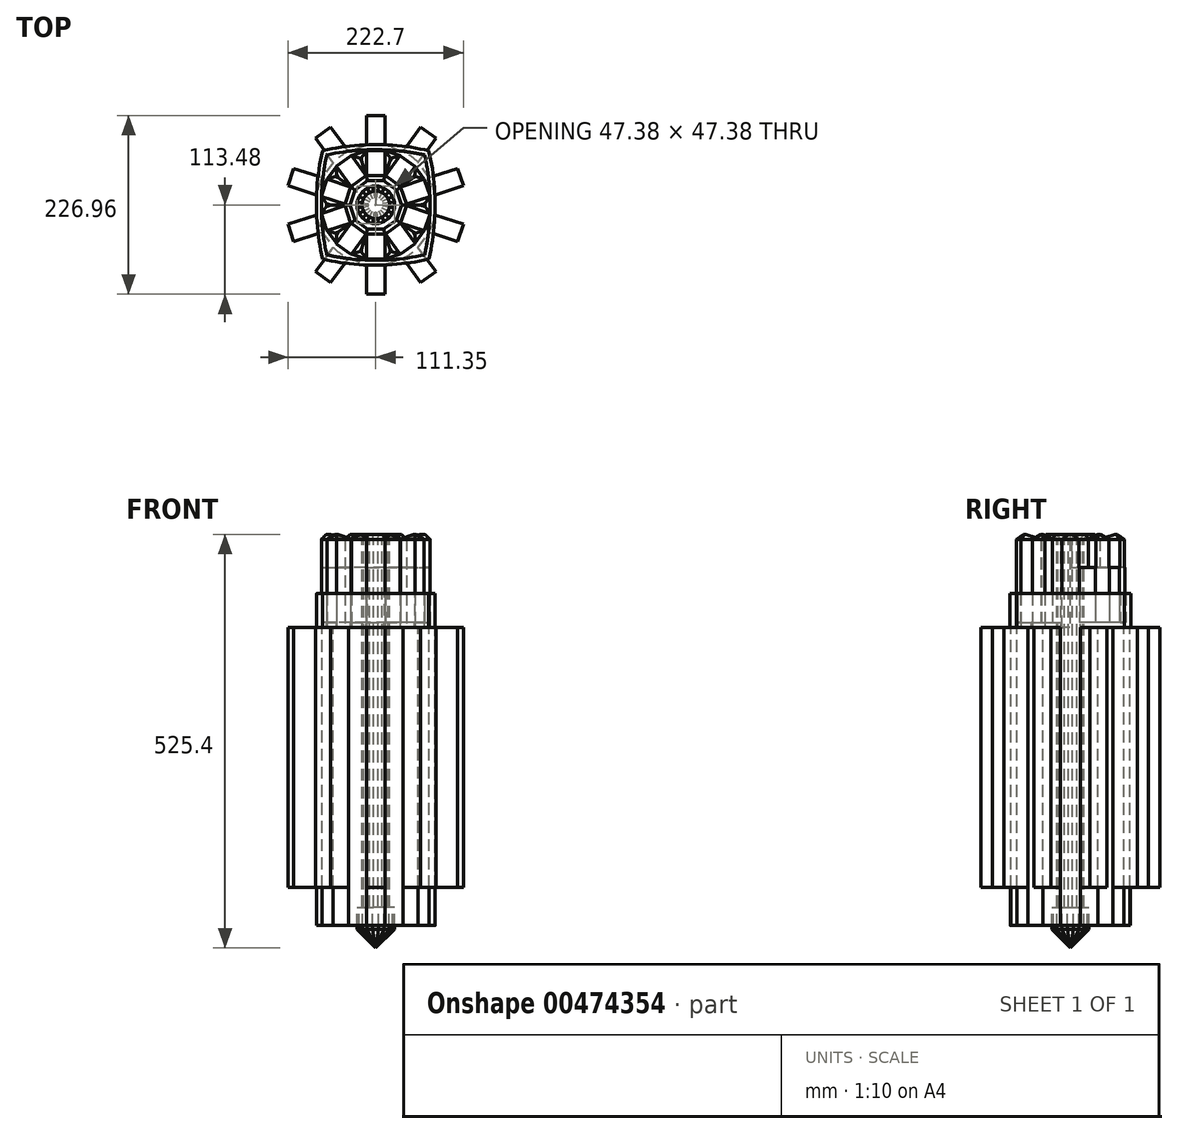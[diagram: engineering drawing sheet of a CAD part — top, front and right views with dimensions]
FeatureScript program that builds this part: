
annotation { "Feature Type Name" : "Feature", "Feature Type Description" : "" }
export const myFeature = defineFeature(function(context is Context, id is Id, definition is map)
    precondition{}
    {
        {
            var Q0;
            Q0=qCreatedBy(makeId("Top.planeOp"),FACE);
            var sketch = newSketch(context, id + "F0", { "sketchPlane" : qUnion([Q0])});
            skEllipse(sketch, "E0", {"center": v(0, 0) * mm, "majorRadius": 152.95 * mm, "minorRadius": 76.53 * mm, "majorAxis": v(1, 0)});
            skEllipse(sketch, "E1", {"center": v(0, 0) * mm, "majorRadius": 153.58 * mm, "minorRadius": 75.38 * mm, "majorAxis": v(0, -1)});
            skEllipse(sketch, "E2", {"center": v(0, 0) * mm, "majorRadius": 194.51 * mm, "minorRadius": 96.8 * mm, "majorAxis": v(0.7, -0.7)});
            skEllipse(sketch, "E3", {"center": v(0, 0) * mm, "majorRadius": 196.36 * mm, "minorRadius": 95.93 * mm, "majorAxis": v(0.7, 0.7)});
            skSolve(sketch);
        }
        {
            var Q0;
            {var subQ0=sQuery(id+"F0.wireOp",EDGE,"E1");var subQ1=sQuery(id+"F0.wireOp",EDGE,"E0");var subQ5=makeQuery(id+"F0.imprint","INTERSECT",VERTEX,{"disambiguationData":[OD(0.0)],"derivedFrom":[subQ1,subQ0]});Q0=makeQuery(id+"F0.imprint","IMPRINT",FACE,{"disambiguationData":[TD([[makeQuery(id+"F0.imprint","IMPRINT",EDGE,{"disambiguationData":[TD([[subQ5,-1.0]])],"derivedFrom":subQ1}),1.0]])]});}
            extrude(context, id + "F1", {"entities" : qUnion([Q0]), "depth" : 127 * mm});
        }
        {
            var Q0;
            Q0=makeQuery(id+"F1.opExtrude","CAP_FACE",FACE,{"disambiguationData":[OSD([sQuery(id+"F0.wireOp",EDGE,"E0"),sQuery(id+"F0.wireOp",EDGE,"E1"),sQuery(id+"F0.wireOp",EDGE,"E3")])],"isStart":true});
            var sketch = newSketch(context, id + "F2", { "sketchPlane" : qUnion([Q0])});
            skCircle(sketch, "E4.cCircle", {"center": v(0, 0) * mm, "radius": 75.38 * mm, "construction": true});
            skLineSegment(sketch, "E4.0", {"start": v(75.38, 11.94) * mm, "end": v(75.38, -11.94) * mm});
            skLineSegment(sketch, "E4.1", {"start": v(75.38, -11.94) * mm, "end": v(68, -34.65) * mm});
            skLineSegment(sketch, "E4.2", {"start": v(68, -34.65) * mm, "end": v(53.96, -53.96) * mm});
            skLineSegment(sketch, "E4.3", {"start": v(53.96, -53.96) * mm, "end": v(34.65, -68) * mm});
            skLineSegment(sketch, "E4.4", {"start": v(34.65, -68) * mm, "end": v(11.94, -75.38) * mm});
            skLineSegment(sketch, "E4.5", {"start": v(11.94, -75.38) * mm, "end": v(-11.94, -75.38) * mm});
            skLineSegment(sketch, "E4.6", {"start": v(-11.94, -75.38) * mm, "end": v(-34.65, -68) * mm});
            skLineSegment(sketch, "E4.7", {"start": v(-34.65, -68) * mm, "end": v(-53.96, -53.96) * mm});
            skLineSegment(sketch, "E4.8", {"start": v(-53.96, -53.96) * mm, "end": v(-68, -34.65) * mm});
            skLineSegment(sketch, "E4.9", {"start": v(-68, -34.65) * mm, "end": v(-75.38, -11.94) * mm});
            skLineSegment(sketch, "E4.10", {"start": v(-75.38, -11.94) * mm, "end": v(-75.38, 11.94) * mm});
            skLineSegment(sketch, "E4.11", {"start": v(-75.38, 11.94) * mm, "end": v(-68, 34.65) * mm});
            skLineSegment(sketch, "E4.12", {"start": v(-68, 34.65) * mm, "end": v(-53.96, 53.96) * mm});
            skLineSegment(sketch, "E4.13", {"start": v(-53.96, 53.96) * mm, "end": v(-34.65, 68) * mm});
            skLineSegment(sketch, "E4.14", {"start": v(-34.65, 68) * mm, "end": v(-11.94, 75.38) * mm});
            skLineSegment(sketch, "E4.15", {"start": v(-11.94, 75.38) * mm, "end": v(11.94, 75.38) * mm});
            skLineSegment(sketch, "E4.16", {"start": v(11.94, 75.38) * mm, "end": v(34.65, 68) * mm});
            skLineSegment(sketch, "E4.17", {"start": v(34.65, 68) * mm, "end": v(53.96, 53.96) * mm});
            skLineSegment(sketch, "E4.18", {"start": v(53.96, 53.96) * mm, "end": v(68, 34.65) * mm});
            skLineSegment(sketch, "E4.19", {"start": v(68, 34.65) * mm, "end": v(75.38, 11.94) * mm});
            skPoint(sketch, "E4.0.midPoint", {"position": v(75.38, 0) * mm});
            skSolve(sketch);
        }
        {
            var Q0;
            {var subQ11=sQuery(id+"F2.wireOp",EDGE,"E4.2");Q0=makeQuery(id+"F2.imprint","IMPRINT",FACE,{"disambiguationData":[TD([[makeQuery(id+"F2.imprint","IMPRINT",EDGE,{"derivedFrom":subQ11}),-1.0]])]});}
            extrude(context, id + "F3", {"entities" : qUnion([Q0]), "operationType" : NewBodyOperationType.ADD, "depth" : 76.2 * mm});
        }
        {
            var Q0;
            Q0=makeQuery(id+"F3.opExtrude","CAP_FACE",FACE,{"disambiguationData":[OSD([sQuery(id+"F0.wireOp",EDGE,"E1"),sQuery(id+"F2.wireOp",EDGE,"E4.1"),sQuery(id+"F2.wireOp",EDGE,"E4.2"),sQuery(id+"F2.wireOp",EDGE,"E4.3"),sQuery(id+"F2.wireOp",EDGE,"E4.4"),sQuery(id+"F2.wireOp",EDGE,"E4.5"),sQuery(id+"F2.wireOp",EDGE,"E4.6"),sQuery(id+"F2.wireOp",EDGE,"E4.7"),sQuery(id+"F2.wireOp",EDGE,"E4.8"),sQuery(id+"F2.wireOp",EDGE,"E4.9"),sQuery(id+"F2.wireOp",EDGE,"E4.11"),sQuery(id+"F2.wireOp",EDGE,"E4.12"),sQuery(id+"F2.wireOp",EDGE,"E4.13"),sQuery(id+"F2.wireOp",EDGE,"E4.14"),sQuery(id+"F2.wireOp",EDGE,"E4.15"),sQuery(id+"F2.wireOp",EDGE,"E4.16"),sQuery(id+"F2.wireOp",EDGE,"E4.17"),sQuery(id+"F2.wireOp",EDGE,"E4.18"),sQuery(id+"F2.wireOp",EDGE,"E4.19")])],"isStart":false});
            var sketch = newSketch(context, id + "F4", { "sketchPlane" : qUnion([Q0])});
            skCircle(sketch, "E5.cCircle", {"center": v(0, 0) * mm, "radius": 23.7 * mm, "construction": true});
            skPoint(sketch, "E5.cCircle.perimeterSnap0", {"position": v(71.56, -23.7) * mm});
            skLineSegment(sketch, "E5.0", {"start": v(3.75, -23.7) * mm, "end": v(-3.75, -23.7) * mm});
            skLineSegment(sketch, "E5.1", {"start": v(-3.75, -23.7) * mm, "end": v(-10.9, -21.37) * mm});
            skLineSegment(sketch, "E5.2", {"start": v(-10.9, -21.37) * mm, "end": v(-16.96, -16.96) * mm});
            skLineSegment(sketch, "E5.3", {"start": v(-16.96, -16.96) * mm, "end": v(-21.37, -10.9) * mm});
            skLineSegment(sketch, "E5.4", {"start": v(-21.37, -10.9) * mm, "end": v(-23.7, -3.75) * mm});
            skLineSegment(sketch, "E5.5", {"start": v(-23.7, -3.75) * mm, "end": v(-23.7, 3.75) * mm});
            skLineSegment(sketch, "E5.6", {"start": v(-23.7, 3.75) * mm, "end": v(-21.37, 10.9) * mm});
            skLineSegment(sketch, "E5.7", {"start": v(-21.37, 10.9) * mm, "end": v(-16.96, 16.96) * mm});
            skLineSegment(sketch, "E5.8", {"start": v(-16.96, 16.96) * mm, "end": v(-10.9, 21.37) * mm});
            skLineSegment(sketch, "E5.9", {"start": v(-10.9, 21.37) * mm, "end": v(-3.75, 23.7) * mm});
            skLineSegment(sketch, "E5.10", {"start": v(-3.75, 23.7) * mm, "end": v(3.75, 23.7) * mm});
            skLineSegment(sketch, "E5.11", {"start": v(3.75, 23.7) * mm, "end": v(10.9, 21.37) * mm});
            skLineSegment(sketch, "E5.12", {"start": v(10.9, 21.37) * mm, "end": v(16.96, 16.96) * mm});
            skLineSegment(sketch, "E5.13", {"start": v(16.96, 16.96) * mm, "end": v(21.37, 10.9) * mm});
            skLineSegment(sketch, "E5.14", {"start": v(21.37, 10.9) * mm, "end": v(23.7, 3.75) * mm});
            skLineSegment(sketch, "E5.15", {"start": v(23.7, 3.75) * mm, "end": v(23.7, -3.75) * mm});
            skLineSegment(sketch, "E5.16", {"start": v(23.7, -3.75) * mm, "end": v(21.37, -10.9) * mm});
            skLineSegment(sketch, "E5.17", {"start": v(21.37, -10.9) * mm, "end": v(16.96, -16.96) * mm});
            skLineSegment(sketch, "E5.18", {"start": v(16.96, -16.96) * mm, "end": v(10.9, -21.37) * mm});
            skLineSegment(sketch, "E5.19", {"start": v(10.9, -21.37) * mm, "end": v(3.75, -23.7) * mm});
            skPoint(sketch, "E5.0.midPoint", {"position": v(0, -23.7) * mm});
            skPoint(sketch, "E5.0.midPoint.positionSnap0", {"position": v(71.56, -23.7) * mm});
            skSolve(sketch);
        }
        {
            var Q0;
            Q0=makeQuery(id+"F4.imprint","IMPRINT",FACE,{"disambiguationData":[TD([[makeQuery(id+"F4.imprint","IMPRINT",EDGE,{"derivedFrom":sQuery(id+"F4.wireOp",EDGE,"E5.0")}),-1.0]])]});
            extrude(context, id + "F5", {"entities" : qUnion([Q0]), "operationType" : NewBodyOperationType.ADD, "depth" : 25.4 * mm});
        }
        {
            var Q0;
            Q0=makeQuery(id+"F5.opExtrude","CAP_FACE",FACE,{"disambiguationData":[OSD([sQuery(id+"F4.wireOp",EDGE,"E5.0"),sQuery(id+"F4.wireOp",EDGE,"E5.1"),sQuery(id+"F4.wireOp",EDGE,"E5.2"),sQuery(id+"F4.wireOp",EDGE,"E5.3"),sQuery(id+"F4.wireOp",EDGE,"E5.4"),sQuery(id+"F4.wireOp",EDGE,"E5.5"),sQuery(id+"F4.wireOp",EDGE,"E5.6"),sQuery(id+"F4.wireOp",EDGE,"E5.7"),sQuery(id+"F4.wireOp",EDGE,"E5.8"),sQuery(id+"F4.wireOp",EDGE,"E5.9"),sQuery(id+"F4.wireOp",EDGE,"E5.10"),sQuery(id+"F4.wireOp",EDGE,"E5.11"),sQuery(id+"F4.wireOp",EDGE,"E5.12"),sQuery(id+"F4.wireOp",EDGE,"E5.13"),sQuery(id+"F4.wireOp",EDGE,"E5.14"),sQuery(id+"F4.wireOp",EDGE,"E5.15"),sQuery(id+"F4.wireOp",EDGE,"E5.16"),sQuery(id+"F4.wireOp",EDGE,"E5.17"),sQuery(id+"F4.wireOp",EDGE,"E5.18"),sQuery(id+"F4.wireOp",EDGE,"E5.19")])],"isStart":false});
            shell(context, id + "F6", {"entities" : qUnion([Q0]), "thickness" : 6.35 * mm});
        }
        {
            var Q0;
            Q0=makeQuery(id+"F3.opExtrude","CAP_FACE",FACE,{"disambiguationData":[OSD([sQuery(id+"F0.wireOp",EDGE,"E1"),sQuery(id+"F2.wireOp",EDGE,"E4.1"),sQuery(id+"F2.wireOp",EDGE,"E4.2"),sQuery(id+"F2.wireOp",EDGE,"E4.3"),sQuery(id+"F2.wireOp",EDGE,"E4.4"),sQuery(id+"F2.wireOp",EDGE,"E4.5"),sQuery(id+"F2.wireOp",EDGE,"E4.6"),sQuery(id+"F2.wireOp",EDGE,"E4.7"),sQuery(id+"F2.wireOp",EDGE,"E4.8"),sQuery(id+"F2.wireOp",EDGE,"E4.9"),sQuery(id+"F2.wireOp",EDGE,"E4.11"),sQuery(id+"F2.wireOp",EDGE,"E4.12"),sQuery(id+"F2.wireOp",EDGE,"E4.13"),sQuery(id+"F2.wireOp",EDGE,"E4.14"),sQuery(id+"F2.wireOp",EDGE,"E4.15"),sQuery(id+"F2.wireOp",EDGE,"E4.16"),sQuery(id+"F2.wireOp",EDGE,"E4.17"),sQuery(id+"F2.wireOp",EDGE,"E4.18"),sQuery(id+"F2.wireOp",EDGE,"E4.19")])],"isStart":false});
            extrude(context, id + "F7", {"entities" : qUnion([Q0]), "operationType" : NewBodyOperationType.ADD, "depth" : 254 * mm});
        }
        {
            var Q0;
            Q0=makeQuery(id+"F5.opExtrude","CAP_FACE",FACE,{"disambiguationData":[OSD([sQuery(id+"F4.wireOp",EDGE,"E5.0"),sQuery(id+"F4.wireOp",EDGE,"E5.1"),sQuery(id+"F4.wireOp",EDGE,"E5.2"),sQuery(id+"F4.wireOp",EDGE,"E5.3"),sQuery(id+"F4.wireOp",EDGE,"E5.4"),sQuery(id+"F4.wireOp",EDGE,"E5.5"),sQuery(id+"F4.wireOp",EDGE,"E5.6"),sQuery(id+"F4.wireOp",EDGE,"E5.7"),sQuery(id+"F4.wireOp",EDGE,"E5.8"),sQuery(id+"F4.wireOp",EDGE,"E5.9"),sQuery(id+"F4.wireOp",EDGE,"E5.10"),sQuery(id+"F4.wireOp",EDGE,"E5.11"),sQuery(id+"F4.wireOp",EDGE,"E5.12"),sQuery(id+"F4.wireOp",EDGE,"E5.13"),sQuery(id+"F4.wireOp",EDGE,"E5.14"),sQuery(id+"F4.wireOp",EDGE,"E5.15"),sQuery(id+"F4.wireOp",EDGE,"E5.16"),sQuery(id+"F4.wireOp",EDGE,"E5.17"),sQuery(id+"F4.wireOp",EDGE,"E5.18"),sQuery(id+"F4.wireOp",EDGE,"E5.19")])],"isStart":false});
            extrude(context, id + "F8", {"entities" : qUnion([Q0]), "operationType" : NewBodyOperationType.ADD, "depth" : 254 * mm});
        }
        {
            var Q0;
            {var subQ0=sQuery(id+"F2.wireOp",EDGE,"E4.5");Q0=makeQuery(id+"F7.boolean.opBoolean","MERGE",FACE,{"derivedFrom":[makeQuery(id+"F3.opExtrude","SWEPT_FACE",FACE,{"disambiguationData":[OSD([subQ0])]}),makeQuery(id+"F7.opExtrude","SWEPT_FACE",FACE,{"disambiguationData":[OSD([subQ0])]})]});}
            var Q1;
            {var subQ0=sQuery(id+"F2.wireOp",EDGE,"E4.15");Q1=makeQuery(id+"F7.boolean.opBoolean","MERGE",FACE,{"derivedFrom":[makeQuery(id+"F3.opExtrude","SWEPT_FACE",FACE,{"disambiguationData":[OSD([subQ0])]}),makeQuery(id+"F7.opExtrude","SWEPT_FACE",FACE,{"disambiguationData":[OSD([subQ0])]})]});}
            extrude(context, id + "F9", {"entities" : qUnion([Q0, Q1]), "operationType" : NewBodyOperationType.ADD, "endBound" : BoundingType.SYMMETRIC, "depth" : 76.2 * mm});
        }
        {
            var Q0;
            {var subQ0=sQuery(id+"F2.wireOp",EDGE,"E4.13");Q0=makeQuery(id+"F7.boolean.opBoolean","MERGE",FACE,{"derivedFrom":[makeQuery(id+"F3.opExtrude","SWEPT_FACE",FACE,{"disambiguationData":[OSD([subQ0])]}),makeQuery(id+"F7.opExtrude","SWEPT_FACE",FACE,{"disambiguationData":[OSD([subQ0])]})]});}
            var Q1;
            {var subQ0=sQuery(id+"F2.wireOp",EDGE,"E4.3");Q1=makeQuery(id+"F7.boolean.opBoolean","MERGE",FACE,{"derivedFrom":[makeQuery(id+"F3.opExtrude","SWEPT_FACE",FACE,{"disambiguationData":[OSD([subQ0])]}),makeQuery(id+"F7.opExtrude","SWEPT_FACE",FACE,{"disambiguationData":[OSD([subQ0])]})]});}
            extrude(context, id + "F10", {"entities" : qUnion([Q0, Q1]), "operationType" : NewBodyOperationType.ADD, "endBound" : BoundingType.SYMMETRIC, "depth" : 76.2 * mm});
        }
        {
            var Q0;
            {var subQ0=sQuery(id+"F2.wireOp",EDGE,"E4.17");Q0=makeQuery(id+"F7.boolean.opBoolean","MERGE",FACE,{"derivedFrom":[makeQuery(id+"F3.opExtrude","SWEPT_FACE",FACE,{"disambiguationData":[OSD([subQ0])]}),makeQuery(id+"F7.opExtrude","SWEPT_FACE",FACE,{"disambiguationData":[OSD([subQ0])]})]});}
            var Q1;
            {var subQ0=sQuery(id+"F2.wireOp",EDGE,"E4.7");Q1=makeQuery(id+"F7.boolean.opBoolean","MERGE",FACE,{"derivedFrom":[makeQuery(id+"F3.opExtrude","SWEPT_FACE",FACE,{"disambiguationData":[OSD([subQ0])]}),makeQuery(id+"F7.opExtrude","SWEPT_FACE",FACE,{"disambiguationData":[OSD([subQ0])]})]});}
            extrude(context, id + "F11", {"entities" : qUnion([Q0, Q1]), "operationType" : NewBodyOperationType.ADD, "endBound" : BoundingType.SYMMETRIC, "depth" : 76.2 * mm});
        }
        {
            var Q0;
            {var subQ0=sQuery(id+"F2.wireOp",EDGE,"E4.9");Q0=makeQuery(id+"F7.boolean.opBoolean","MERGE",FACE,{"derivedFrom":[makeQuery(id+"F3.opExtrude","SWEPT_FACE",FACE,{"disambiguationData":[OSD([subQ0])]}),makeQuery(id+"F7.opExtrude","SWEPT_FACE",FACE,{"disambiguationData":[OSD([subQ0])]})]});}
            var Q1;
            {var subQ0=sQuery(id+"F2.wireOp",EDGE,"E4.19");Q1=makeQuery(id+"F7.boolean.opBoolean","MERGE",FACE,{"derivedFrom":[makeQuery(id+"F3.opExtrude","SWEPT_FACE",FACE,{"disambiguationData":[OSD([subQ0])]}),makeQuery(id+"F7.opExtrude","SWEPT_FACE",FACE,{"disambiguationData":[OSD([subQ0])]})]});}
            extrude(context, id + "F12", {"entities" : qUnion([Q0, Q1]), "operationType" : NewBodyOperationType.ADD, "endBound" : BoundingType.SYMMETRIC, "depth" : 76.2 * mm});
        }
        {
            var Q0;
            {var subQ0=sQuery(id+"F2.wireOp",EDGE,"E4.11");Q0=makeQuery(id+"F7.boolean.opBoolean","MERGE",FACE,{"derivedFrom":[makeQuery(id+"F3.opExtrude","SWEPT_FACE",FACE,{"disambiguationData":[OSD([subQ0])]}),makeQuery(id+"F7.opExtrude","SWEPT_FACE",FACE,{"disambiguationData":[OSD([subQ0])]})]});}
            var Q1;
            {var subQ0=sQuery(id+"F2.wireOp",EDGE,"E4.1");Q1=makeQuery(id+"F7.boolean.opBoolean","MERGE",FACE,{"derivedFrom":[makeQuery(id+"F3.opExtrude","SWEPT_FACE",FACE,{"disambiguationData":[OSD([subQ0])]}),makeQuery(id+"F7.opExtrude","SWEPT_FACE",FACE,{"disambiguationData":[OSD([subQ0])]})]});}
            extrude(context, id + "F13", {"entities" : qUnion([Q0, Q1]), "operationType" : NewBodyOperationType.ADD, "endBound" : BoundingType.SYMMETRIC, "depth" : 76.2 * mm});
        }
        {
            var Q0;
            Q0=makeQuery(id+"F1.opExtrude","CAP_FACE",FACE,{"disambiguationData":[OSD([sQuery(id+"F0.wireOp",EDGE,"E0"),sQuery(id+"F0.wireOp",EDGE,"E1"),sQuery(id+"F0.wireOp",EDGE,"E3")])],"isStart":false});
            extrude(context, id + "F14", {"entities" : qUnion([Q0]), "operationType" : NewBodyOperationType.REMOVE, "endBound" : BoundingType.SYMMETRIC, "oppositeDirection" : true, "depth" : 168.38 * mm});
        }
        {
            var Q0;
            {var subQ0=sQuery(id+"F2.wireOp",EDGE,"E4.3");var subQ1=sQuery(id+"F2.wireOp",EDGE,"E4.2");Q0=makeQuery(id+"F10.boolean.opBoolean","SPLIT",FACE,{"disambiguationData":[TD([makeQuery(id+"F6.opShell","OFFSET_FACE",FACE,{"disambiguationData":[OSD([subQ1])]})])],"derivedFrom":makeQuery(id+"F10.opExtrude","SWEPT_FACE",FACE,{"disambiguationData":[OSD([subQ0]),TDD([makeQuery(id+"F3.opExtrude","CAP_EDGE",EDGE,{"disambiguationData":[OSD([subQ0])],"isStart":true})])]})});}
            var Q1;
            {var subQ0=sQuery(id+"F2.wireOp",EDGE,"E4.5");var subQ1=sQuery(id+"F2.wireOp",EDGE,"E4.4");Q1=makeQuery(id+"F9.boolean.opBoolean","SPLIT",FACE,{"disambiguationData":[TD([makeQuery(id+"F6.opShell","OFFSET_FACE",FACE,{"disambiguationData":[OSD([subQ1])]})])],"derivedFrom":makeQuery(id+"F9.opExtrude","SWEPT_FACE",FACE,{"disambiguationData":[OSD([subQ0]),TDD([makeQuery(id+"F3.opExtrude","CAP_EDGE",EDGE,{"disambiguationData":[OSD([subQ0])],"isStart":true})])]})});}
            var Q2;
            {var subQ1=sQuery(id+"F2.wireOp",EDGE,"E4.7");var subQ2=sQuery(id+"F2.wireOp",EDGE,"E4.6");Q2=makeQuery(id+"F11.boolean.opBoolean","SPLIT",FACE,{"disambiguationData":[TD([makeQuery(id+"F6.opShell","OFFSET_FACE",FACE,{"disambiguationData":[OSD([subQ2])]})])],"derivedFrom":makeQuery(id+"F11.opExtrude","SWEPT_FACE",FACE,{"disambiguationData":[OSD([subQ1]),TDD([makeQuery(id+"F3.opExtrude","CAP_EDGE",EDGE,{"disambiguationData":[OSD([subQ1])],"isStart":true})])]})});}
            var Q3;
            {var subQ4=sQuery(id+"F2.wireOp",EDGE,"E4.9");var subQ5=sQuery(id+"F2.wireOp",EDGE,"E4.8");Q3=makeQuery(id+"F12.boolean.opBoolean","SPLIT",FACE,{"disambiguationData":[TD([makeQuery(id+"F6.opShell","OFFSET_FACE",FACE,{"disambiguationData":[OSD([subQ5])]})])],"derivedFrom":makeQuery(id+"F12.opExtrude","SWEPT_FACE",FACE,{"disambiguationData":[OSD([subQ4]),TDD([makeQuery(id+"F3.opExtrude","CAP_EDGE",EDGE,{"disambiguationData":[OSD([subQ4])],"isStart":true})])]})});}
            var Q4;
            {var subQ1=sQuery(id+"F2.wireOp",EDGE,"E4.15");var subQ2=sQuery(id+"F2.wireOp",EDGE,"E4.14");Q4=makeQuery(id+"F9.boolean.opBoolean","SPLIT",FACE,{"disambiguationData":[TD([makeQuery(id+"F6.opShell","OFFSET_FACE",FACE,{"disambiguationData":[OSD([subQ2])]})])],"derivedFrom":makeQuery(id+"F9.opExtrude","SWEPT_FACE",FACE,{"disambiguationData":[OSD([subQ1]),TDD([makeQuery(id+"F3.opExtrude","CAP_EDGE",EDGE,{"disambiguationData":[OSD([subQ1])],"isStart":true})])]})});}
            var Q5;
            {var subQ0=sQuery(id+"F2.wireOp",EDGE,"E4.17");var subQ1=sQuery(id+"F2.wireOp",EDGE,"E4.16");Q5=makeQuery(id+"F11.boolean.opBoolean","SPLIT",FACE,{"disambiguationData":[TD([makeQuery(id+"F6.opShell","OFFSET_FACE",FACE,{"disambiguationData":[OSD([subQ1])]})])],"derivedFrom":makeQuery(id+"F11.opExtrude","SWEPT_FACE",FACE,{"disambiguationData":[OSD([subQ0]),TDD([makeQuery(id+"F3.opExtrude","CAP_EDGE",EDGE,{"disambiguationData":[OSD([subQ0])],"isStart":true})])]})});}
            var Q6;
            {var subQ1=sQuery(id+"F2.wireOp",EDGE,"E4.11");Q6=makeQuery(id+"F13.boolean.opBoolean","SPLIT",FACE,{"disambiguationData":[TD([makeQuery(id+"F6.opShell","OFFSET_FACE",FACE,{"disambiguationData":[OSD([subQ1])]})])],"derivedFrom":makeQuery(id+"F13.opExtrude","SWEPT_FACE",FACE,{"disambiguationData":[OSD([subQ1]),TDD([makeQuery(id+"F3.opExtrude","CAP_EDGE",EDGE,{"disambiguationData":[OSD([subQ1])],"isStart":true})])]})});}
            var Q7;
            {var subQ1=sQuery(id+"F2.wireOp",EDGE,"E4.13");var subQ2=sQuery(id+"F2.wireOp",EDGE,"E4.12");Q7=makeQuery(id+"F10.boolean.opBoolean","SPLIT",FACE,{"disambiguationData":[TD([makeQuery(id+"F6.opShell","OFFSET_FACE",FACE,{"disambiguationData":[OSD([subQ2])]})])],"derivedFrom":makeQuery(id+"F10.opExtrude","SWEPT_FACE",FACE,{"disambiguationData":[OSD([subQ1]),TDD([makeQuery(id+"F3.opExtrude","CAP_EDGE",EDGE,{"disambiguationData":[OSD([subQ1])],"isStart":true})])]})});}
            var Q8;
            {var subQ1=sQuery(id+"F2.wireOp",EDGE,"E4.1");Q8=makeQuery(id+"F13.boolean.opBoolean","SPLIT",FACE,{"disambiguationData":[TD([makeQuery(id+"F6.opShell","OFFSET_FACE",FACE,{"disambiguationData":[OSD([subQ1])]})])],"derivedFrom":makeQuery(id+"F13.opExtrude","SWEPT_FACE",FACE,{"disambiguationData":[OSD([subQ1]),TDD([makeQuery(id+"F3.opExtrude","CAP_EDGE",EDGE,{"disambiguationData":[OSD([subQ1])],"isStart":true})])]})});}
            var Q9;
            {var subQ0=sQuery(id+"F2.wireOp",EDGE,"E4.19");var subQ1=sQuery(id+"F2.wireOp",EDGE,"E4.18");Q9=makeQuery(id+"F12.boolean.opBoolean","SPLIT",FACE,{"disambiguationData":[TD([makeQuery(id+"F6.opShell","OFFSET_FACE",FACE,{"disambiguationData":[OSD([subQ1])]})])],"derivedFrom":makeQuery(id+"F12.opExtrude","SWEPT_FACE",FACE,{"disambiguationData":[OSD([subQ0]),TDD([makeQuery(id+"F3.opExtrude","CAP_EDGE",EDGE,{"disambiguationData":[OSD([subQ0])],"isStart":true})])]})});}
            extrude(context, id + "F15", {"entities" : qUnion([Q0, Q1, Q2, Q3, Q4, Q5, Q6, Q7, Q8, Q9]), "operationType" : NewBodyOperationType.ADD, "depth" : 71.7 * mm});
        }
        {
            var Q0;
            Q0=makeQuery(id+"F6.opShell","OFFSET_FACE",FACE,{"disambiguationData":[OSD([sQuery(id+"F0.wireOp",EDGE,"E1"),sQuery(id+"F2.wireOp",EDGE,"E4.1"),sQuery(id+"F2.wireOp",EDGE,"E4.2"),sQuery(id+"F2.wireOp",EDGE,"E4.3"),sQuery(id+"F2.wireOp",EDGE,"E4.4"),sQuery(id+"F2.wireOp",EDGE,"E4.5"),sQuery(id+"F2.wireOp",EDGE,"E4.6"),sQuery(id+"F2.wireOp",EDGE,"E4.7"),sQuery(id+"F2.wireOp",EDGE,"E4.8"),sQuery(id+"F2.wireOp",EDGE,"E4.9"),sQuery(id+"F2.wireOp",EDGE,"E4.11"),sQuery(id+"F2.wireOp",EDGE,"E4.12"),sQuery(id+"F2.wireOp",EDGE,"E4.13"),sQuery(id+"F2.wireOp",EDGE,"E4.14"),sQuery(id+"F2.wireOp",EDGE,"E4.15"),sQuery(id+"F2.wireOp",EDGE,"E4.16"),sQuery(id+"F2.wireOp",EDGE,"E4.17"),sQuery(id+"F2.wireOp",EDGE,"E4.18"),sQuery(id+"F2.wireOp",EDGE,"E4.19")])]});
            extrude(context, id + "F16", {"entities" : qUnion([Q0]), "operationType" : NewBodyOperationType.ADD, "endBound" : BoundingType.SYMMETRIC, "depth" : 376 * mm});
        }
        {
            var Q0;
            Q0=makeQuery(id+"F15.opExtrude","CAP_FACE",FACE,{"disambiguationData":[OSD([sQuery(id+"F2.wireOp",EDGE,"E4.9")])],"isStart":false});
            var Q1;
            Q1=makeQuery(id+"F15.opExtrude","CAP_FACE",FACE,{"disambiguationData":[OSD([sQuery(id+"F2.wireOp",EDGE,"E4.3")])],"isStart":false});
            var Q2;
            Q2=makeQuery(id+"F15.opExtrude","CAP_FACE",FACE,{"disambiguationData":[OSD([sQuery(id+"F2.wireOp",EDGE,"E4.17")])],"isStart":false});
            var Q3;
            Q3=makeQuery(id+"F15.opExtrude","CAP_FACE",FACE,{"disambiguationData":[OSD([sQuery(id+"F2.wireOp",EDGE,"E4.11")])],"isStart":false});
            var Q4;
            Q4=makeQuery(id+"F15.opExtrude","CAP_FACE",FACE,{"disambiguationData":[OSD([sQuery(id+"F2.wireOp",EDGE,"E4.13")])],"isStart":false});
            var Q5;
            Q5=makeQuery(id+"F15.opExtrude","CAP_FACE",FACE,{"disambiguationData":[OSD([sQuery(id+"F2.wireOp",EDGE,"E4.15")])],"isStart":false});
            var Q6;
            Q6=makeQuery(id+"F15.opExtrude","CAP_FACE",FACE,{"disambiguationData":[OSD([sQuery(id+"F2.wireOp",EDGE,"E4.1")])],"isStart":false});
            var Q7;
            Q7=makeQuery(id+"F15.opExtrude","CAP_FACE",FACE,{"disambiguationData":[OSD([sQuery(id+"F2.wireOp",EDGE,"E4.19")])],"isStart":false});
            var Q8;
            Q8=makeQuery(id+"F15.opExtrude","CAP_FACE",FACE,{"disambiguationData":[OSD([sQuery(id+"F2.wireOp",EDGE,"E4.5")])],"isStart":false});
            var Q9;
            Q9=makeQuery(id+"F15.opExtrude","CAP_FACE",FACE,{"disambiguationData":[OSD([sQuery(id+"F2.wireOp",EDGE,"E4.7")])],"isStart":false});
            extrude(context, id + "F17", {"entities" : qUnion([Q0, Q1, Q2, Q3, Q4, Q5, Q6, Q7, Q8, Q9]), "operationType" : NewBodyOperationType.ADD, "endBound" : BoundingType.SYMMETRIC, "depth" : 8.15 * mm});
        }
        {
            var Q0;
            {var subQ0=sQuery(id+"F2.wireOp",EDGE,"E4.11");var subQ1=sQuery(id+"F2.wireOp",EDGE,"E4.1");var subQ2=sQuery(id+"F2.wireOp",EDGE,"E4.19");var subQ3=sQuery(id+"F2.wireOp",EDGE,"E4.9");var subQ4=sQuery(id+"F2.wireOp",EDGE,"E4.17");var subQ5=sQuery(id+"F2.wireOp",EDGE,"E4.7");var subQ6=sQuery(id+"F2.wireOp",EDGE,"E4.13");var subQ7=sQuery(id+"F2.wireOp",EDGE,"E4.3");var subQ8=sQuery(id+"F2.wireOp",EDGE,"E4.15");var subQ9=sQuery(id+"F2.wireOp",EDGE,"E4.5");Q0=makeQuery(id+"F13.boolean.opBoolean","MERGE",FACE,{"derivedFrom":[makeQuery(id+"F12.boolean.opBoolean","MERGE",FACE,{"derivedFrom":[makeQuery(id+"F11.boolean.opBoolean","MERGE",FACE,{"derivedFrom":[makeQuery(id+"F10.boolean.opBoolean","MERGE",FACE,{"derivedFrom":[makeQuery(id+"F9.boolean.opBoolean","MERGE",FACE,{"derivedFrom":[makeQuery(id+"F7.opExtrude","CAP_FACE",FACE,{"disambiguationData":[OSD([sQuery(id+"F0.wireOp",EDGE,"E1"),subQ1,sQuery(id+"F2.wireOp",EDGE,"E4.2"),subQ7,sQuery(id+"F2.wireOp",EDGE,"E4.4"),subQ9,sQuery(id+"F2.wireOp",EDGE,"E4.6"),subQ5,sQuery(id+"F2.wireOp",EDGE,"E4.8"),subQ3,subQ0,sQuery(id+"F2.wireOp",EDGE,"E4.12"),subQ6,sQuery(id+"F2.wireOp",EDGE,"E4.14"),subQ8,sQuery(id+"F2.wireOp",EDGE,"E4.16"),subQ4,sQuery(id+"F2.wireOp",EDGE,"E4.18"),subQ2])],"isStart":false}),makeQuery(id+"F9.opExtrude","SWEPT_FACE",FACE,{"disambiguationData":[OSD([subQ9]),TDD([makeQuery(id+"F7.opExtrude","CAP_EDGE",EDGE,{"disambiguationData":[OSD([subQ9])],"isStart":false})])]}),makeQuery(id+"F9.opExtrude","SWEPT_FACE",FACE,{"disambiguationData":[OSD([subQ8]),TDD([makeQuery(id+"F7.opExtrude","CAP_EDGE",EDGE,{"disambiguationData":[OSD([subQ8])],"isStart":false})])]})]}),makeQuery(id+"F10.opExtrude","SWEPT_FACE",FACE,{"disambiguationData":[OSD([subQ7]),TDD([makeQuery(id+"F7.opExtrude","CAP_EDGE",EDGE,{"disambiguationData":[OSD([subQ7])],"isStart":false})])]}),makeQuery(id+"F10.opExtrude","SWEPT_FACE",FACE,{"disambiguationData":[OSD([subQ6]),TDD([makeQuery(id+"F7.opExtrude","CAP_EDGE",EDGE,{"disambiguationData":[OSD([subQ6])],"isStart":false})])]})]}),makeQuery(id+"F11.opExtrude","SWEPT_FACE",FACE,{"disambiguationData":[OSD([subQ5]),TDD([makeQuery(id+"F7.opExtrude","CAP_EDGE",EDGE,{"disambiguationData":[OSD([subQ5])],"isStart":false})])]}),makeQuery(id+"F11.opExtrude","SWEPT_FACE",FACE,{"disambiguationData":[OSD([subQ4]),TDD([makeQuery(id+"F7.opExtrude","CAP_EDGE",EDGE,{"disambiguationData":[OSD([subQ4])],"isStart":false})])]})]}),makeQuery(id+"F12.opExtrude","SWEPT_FACE",FACE,{"disambiguationData":[OSD([subQ3]),TDD([makeQuery(id+"F7.opExtrude","CAP_EDGE",EDGE,{"disambiguationData":[OSD([subQ3])],"isStart":false})])]}),makeQuery(id+"F12.opExtrude","SWEPT_FACE",FACE,{"disambiguationData":[OSD([subQ2]),TDD([makeQuery(id+"F7.opExtrude","CAP_EDGE",EDGE,{"disambiguationData":[OSD([subQ2])],"isStart":false})])]})]}),makeQuery(id+"F13.opExtrude","SWEPT_FACE",FACE,{"disambiguationData":[OSD([subQ1]),TDD([makeQuery(id+"F7.opExtrude","CAP_EDGE",EDGE,{"disambiguationData":[OSD([subQ1])],"isStart":false})])]}),makeQuery(id+"F13.opExtrude","SWEPT_FACE",FACE,{"disambiguationData":[OSD([subQ0]),TDD([makeQuery(id+"F7.opExtrude","CAP_EDGE",EDGE,{"disambiguationData":[OSD([subQ0])],"isStart":false})])]})]});}
            var sketch = newSketch(context, id + "F18", { "sketchPlane" : qUnion([Q0])});
            skCircle(sketch, "E6", {"center": v(0, 0) * mm, "radius": 76.32 * mm});
            skPoint(sketch, "E6.first.point", {"position": v(11.94, 75.38) * mm});
            skPoint(sketch, "E6.second.point", {"position": v(68, -34.65) * mm});
            skPoint(sketch, "E6.third.point", {"position": v(-53.96, -53.96) * mm});
            skSolve(sketch);
        }
        {
            var Q0;
            {var subQ24=sQuery(id+"F2.wireOp",EDGE,"E4.2");var subQ25=makeQuery(id+"F7.opExtrude","CAP_EDGE",EDGE,{"disambiguationData":[OSD([subQ24])],"isStart":false});Q0=makeQuery(id+"F18.imprint","IMPRINT",FACE,{"disambiguationData":[TD([[makeQuery(id+"F18.imprint","IMPRINT",EDGE,{"derivedFrom":subQ25}),-1.0]])]});}
            extrude(context, id + "F19", {"entities" : qUnion([Q0]), "operationType" : NewBodyOperationType.ADD, "depth" : 48.58 * mm});
        }
        {
            var Q0;
            Q0=makeQuery(id+"F19.opExtrude","CAP_FACE",FACE,{"disambiguationData":[OSD([sQuery(id+"F0.wireOp",EDGE,"E1"),sQuery(id+"F2.wireOp",EDGE,"E4.1"),sQuery(id+"F2.wireOp",EDGE,"E4.2"),sQuery(id+"F2.wireOp",EDGE,"E4.4"),sQuery(id+"F2.wireOp",EDGE,"E4.6"),sQuery(id+"F2.wireOp",EDGE,"E4.8"),sQuery(id+"F2.wireOp",EDGE,"E4.9"),sQuery(id+"F2.wireOp",EDGE,"E4.11"),sQuery(id+"F2.wireOp",EDGE,"E4.12"),sQuery(id+"F2.wireOp",EDGE,"E4.14"),sQuery(id+"F2.wireOp",EDGE,"E4.16"),sQuery(id+"F2.wireOp",EDGE,"E4.18"),sQuery(id+"F2.wireOp",EDGE,"E4.19"),sQuery(id+"F4.wireOp",EDGE,"E5.0"),sQuery(id+"F4.wireOp",EDGE,"E5.1"),sQuery(id+"F4.wireOp",EDGE,"E5.2"),sQuery(id+"F4.wireOp",EDGE,"E5.3"),sQuery(id+"F4.wireOp",EDGE,"E5.4"),sQuery(id+"F4.wireOp",EDGE,"E5.5"),sQuery(id+"F4.wireOp",EDGE,"E5.6"),sQuery(id+"F4.wireOp",EDGE,"E5.7"),sQuery(id+"F4.wireOp",EDGE,"E5.8"),sQuery(id+"F4.wireOp",EDGE,"E5.9"),sQuery(id+"F4.wireOp",EDGE,"E5.10"),sQuery(id+"F4.wireOp",EDGE,"E5.11"),sQuery(id+"F4.wireOp",EDGE,"E5.12"),sQuery(id+"F4.wireOp",EDGE,"E5.13"),sQuery(id+"F4.wireOp",EDGE,"E5.14"),sQuery(id+"F4.wireOp",EDGE,"E5.15"),sQuery(id+"F4.wireOp",EDGE,"E5.16"),sQuery(id+"F4.wireOp",EDGE,"E5.17"),sQuery(id+"F4.wireOp",EDGE,"E5.18"),sQuery(id+"F4.wireOp",EDGE,"E5.19"),sQuery(id+"F18.wireOp",EDGE,"E6")])],"isStart":false});
            var sketch = newSketch(context, id + "F20", { "sketchPlane" : qUnion([Q0])});
            skCircle(sketch, "E7", {"center": v(0, 0) * mm, "radius": 23.99 * mm});
            skSolve(sketch);
        }
        {
            var Q0;
            Q0=makeQuery(id+"F20.imprint","IMPRINT",FACE,{"disambiguationData":[TD([[makeQuery(id+"F20.imprint","IMPRINT",EDGE,{"derivedFrom":makeQuery(id+"F19.opExtrude","CAP_EDGE",EDGE,{"disambiguationData":[OSD([sQuery(id+"F4.wireOp",EDGE,"E5.0")])],"isStart":false})}),-1.0]])]});
            extrude(context, id + "F21", {"entities" : qUnion([Q0]), "depth" : 28.48 * mm});
        }
        {
            var Q0;
            Q0=makeQuery(id+"F16.opExtrude","CAP_FACE",FACE,{"disambiguationData":[OSD([sQuery(id+"F0.wireOp",EDGE,"E1"),sQuery(id+"F2.wireOp",EDGE,"E4.1"),sQuery(id+"F2.wireOp",EDGE,"E4.2"),sQuery(id+"F2.wireOp",EDGE,"E4.3"),sQuery(id+"F2.wireOp",EDGE,"E4.4"),sQuery(id+"F2.wireOp",EDGE,"E4.5"),sQuery(id+"F2.wireOp",EDGE,"E4.6"),sQuery(id+"F2.wireOp",EDGE,"E4.7"),sQuery(id+"F2.wireOp",EDGE,"E4.8"),sQuery(id+"F2.wireOp",EDGE,"E4.9"),sQuery(id+"F2.wireOp",EDGE,"E4.11"),sQuery(id+"F2.wireOp",EDGE,"E4.12"),sQuery(id+"F2.wireOp",EDGE,"E4.13"),sQuery(id+"F2.wireOp",EDGE,"E4.14"),sQuery(id+"F2.wireOp",EDGE,"E4.15"),sQuery(id+"F2.wireOp",EDGE,"E4.16"),sQuery(id+"F2.wireOp",EDGE,"E4.17"),sQuery(id+"F2.wireOp",EDGE,"E4.18"),sQuery(id+"F2.wireOp",EDGE,"E4.19")])],"isStart":false});
            chamfer(context, id + "F22", {"entities" : qUnion([Q0]), "width" : 6.35 * mm, "tangentPropagation" : true});
        }
        {
            var Q0;
            Q0=makeQuery(id+"F21.opExtrude","CAP_FACE",FACE,{"disambiguationData":[OSD([sQuery(id+"F4.wireOp",EDGE,"E5.0"),sQuery(id+"F4.wireOp",EDGE,"E5.1"),sQuery(id+"F4.wireOp",EDGE,"E5.2"),sQuery(id+"F4.wireOp",EDGE,"E5.3"),sQuery(id+"F4.wireOp",EDGE,"E5.4"),sQuery(id+"F4.wireOp",EDGE,"E5.5"),sQuery(id+"F4.wireOp",EDGE,"E5.6"),sQuery(id+"F4.wireOp",EDGE,"E5.7"),sQuery(id+"F4.wireOp",EDGE,"E5.8"),sQuery(id+"F4.wireOp",EDGE,"E5.9"),sQuery(id+"F4.wireOp",EDGE,"E5.10"),sQuery(id+"F4.wireOp",EDGE,"E5.11"),sQuery(id+"F4.wireOp",EDGE,"E5.12"),sQuery(id+"F4.wireOp",EDGE,"E5.13"),sQuery(id+"F4.wireOp",EDGE,"E5.14"),sQuery(id+"F4.wireOp",EDGE,"E5.15"),sQuery(id+"F4.wireOp",EDGE,"E5.16"),sQuery(id+"F4.wireOp",EDGE,"E5.17"),sQuery(id+"F4.wireOp",EDGE,"E5.18"),sQuery(id+"F4.wireOp",EDGE,"E5.19")])],"isStart":false});
            chamfer(context, id + "F23", {"entities" : qUnion([Q0]), "width" : 23.62 * mm, "tangentPropagation" : true});
        }
    });
